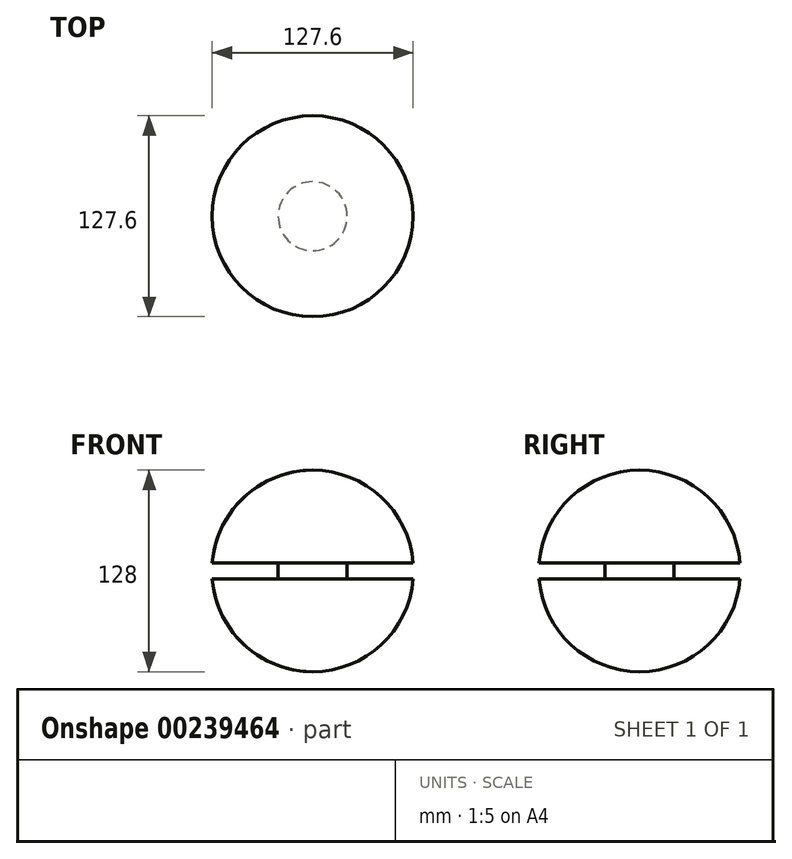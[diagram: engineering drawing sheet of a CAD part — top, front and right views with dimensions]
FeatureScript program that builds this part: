
annotation { "Feature Type Name" : "Feature", "Feature Type Description" : "" }
export const myFeature = defineFeature(function(context is Context, id is Id, definition is map)
    precondition{}
    {
        {
            var Q0;
            Q0=qCreatedBy(makeId("Front.planeOp"),FACE);
            var sketch = newSketch(context, id + "F0", { "sketchPlane" : qUnion([Q0])});
            skArc(sketch, "E0", {"start": v(0, -64) * mm, "mid": v(64, 0) * mm, "end": v(0, 64) * mm});
            skLineSegment(sketch, "E1", {"start": v(0, -64) * mm, "end": v(0, 64) * mm});
            skSolve(sketch);
        }
        {
            var Q0;
            Q0=makeQuery(id+"F0.imprint","IMPRINT",FACE,{"disambiguationData":[TD([[makeQuery(id+"F0.imprint","IMPRINT",EDGE,{"derivedFrom":sQuery(id+"F0.wireOp",EDGE,"E0")}),1.0]])]});
            var Q1;
            Q1=sQuery(id+"F0.wireOp",EDGE,"E1");
            revolve(context, id + "F1", {"entities" : qUnion([Q0]), "axis" : qUnion([Q1]), "revolveType" : RevolveType.FULL});
        }
        {
            var Q0;
            Q0=qCreatedBy(makeId("Front.planeOp"),FACE);
            var sketch = newSketch(context, id + "F2", { "sketchPlane" : qUnion([Q0])});
            skLineSegment(sketch, "E2", {"start": v(0, 63.95) * mm, "end": v(0, -63.75) * mm, "construction": true});
            skSolve(sketch);
        }
        {
            var Q0;
            Q0=qCreatedBy(makeId("Front.planeOp"),FACE);
            var sketch = newSketch(context, id + "F3", { "sketchPlane" : qUnion([Q0])});
            skLineSegment(sketch, "E3.bottom", {"start": v(72.86, 5) * mm, "end": v(21.94, 5) * mm});
            skLineSegment(sketch, "E3.top", {"start": v(72.86, -5) * mm, "end": v(21.94, -5) * mm});
            skLineSegment(sketch, "E3.left", {"start": v(72.86, 5) * mm, "end": v(72.86, -5) * mm});
            skLineSegment(sketch, "E3.right", {"start": v(21.94, 5) * mm, "end": v(21.94, -5) * mm});
            skPoint(sketch, "E3.middle", {"position": v(47.4, 0) * mm});
            skSolve(sketch);
        }
        {
            var Q0;
            Q0 = qSketchRegion(id + "F3", true);
            var Q1;
            Q1=sQuery(id+"F2.wireOp",EDGE,"E2");
            revolve(context, id + "F4", {"operationType" : NewBodyOperationType.REMOVE, "entities" : qUnion([Q0]), "axis" : qUnion([Q1]), "revolveType" : RevolveType.FULL, "oppositeDirection" : true});
        }
    });
